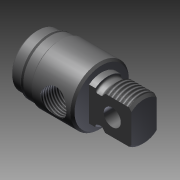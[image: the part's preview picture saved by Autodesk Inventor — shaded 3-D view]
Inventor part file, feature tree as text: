
AUTODESK INVENTOR PART (.ipt)
format: ipt  version: 2011 SP1 (Build 150282100, 282)  size: 287,744 bytes
history: native  units: in
note: dims shown in document units (in); Inventor stores cm internally (conversion verified against a paired STEP export)
features: other x154, sketch x7, revolve x4, thread x2, extrude x2, hole x1
ambient origin geometry x8: Origin, YZ Plane, XZ Plane, XY Plane, X Axis, Y Axis, Z Axis, Center Point
bodies: Solid1 (feature_tree)
feature tree (170):
  revolve  "Revolution1"  Angle=360.0deg
  revolve  "Revolution2"  [1 undecoded]
  thread  "Thread1"  [1 undecoded]
  extrude  "Extrusion1"  TaperAngle=360.0deg  [1 undecoded]
  hole  "Hole1"  [1 undecoded]
  revolve  "Revolution3"  [1 undecoded]
  thread  "Thread2"  [1 undecoded]
  revolve  "Revolution4"  [1 undecoded]
  extrude  "Extrusion2"  [1 undecoded]
  other  "1_XY"
  other  "1_YZ"
  other  "1_ZX"
  other  "1_X"
  other  "1_Y"
  other  "1_Z"
  other  "1_Center"
  other  "c1_XY"
  other  "c1_YZ"
  other  "c1_ZX"
  other  "c1_X"
  other  "c1_Y"
  other  "c1_Z"
  other  "c1_Center"
  other  "c2_XY"
  other  "c2_YZ"
  other  "c2_ZX"
  other  "c2_X"
  other  "c2_Y"
  other  "c2_Z"
  other  "c2_Center"
  other  "cc1_XY"
  other  "cc1_YZ"
  other  "cc1_ZX"
  other  "cc1_X"
  other  "cc1_Y"
  other  "cc1_Z"
  other  "cc1_Center"
  other  "cc2_XY"
  other  "cc2_YZ"
  other  "cc2_ZX"
  other  "cc2_X"
  other  "cc2_Y"
  other  "cc2_Z"
  other  "cc2_Center"
  other  "lovra1_XY"
  other  "lovra1_YZ"
  other  "lovra1_ZX"
  other  "lovra1_X"
  other  "lovra1_Y"
  other  "lovra1_Z"
  other  "lovra1_Center"
  other  "lovra2_XY"
  other  "lovra2_YZ"
  other  "lovra2_ZX"
  other  "lovra2_X"
  other  "lovra2_Y"
  other  "lovra2_Z"
  other  "lovra2_Center"
  other  "lovra21_XY"
  other  "lovra21_YZ"
  other  "lovra21_ZX"
  other  "lovra21_X"
  other  "lovra21_Y"
  other  "lovra21_Z"
  other  "lovra21_Center"
  other  "lovra22_XY"
  other  "lovra22_YZ"
  other  "lovra22_ZX"
  other  "lovra22_X"
  other  "lovra22_Y"
  other  "lovra22_Z"
  other  "lovra22_Center"
  other  "lovra3_XY"
  other  "lovra3_YZ"
  other  "lovra3_ZX"
  other  "lovra3_X"
  other  "lovra3_Y"
  other  "lovra3_Z"
  other  "lovra3_Center"
  other  "olen_XY"
  other  "olen_YZ"
  other  "olen_ZX"
  other  "olen_X"
  other  "olen_Y"
  other  "olen_Z"
  other  "olen_Center"
  other  "p1_XY"
  other  "p1_YZ"
  other  "p1_ZX"
  other  "p1_X"
  other  "p1_Y"
  other  "p1_Z"
  other  "p1_Center"
  other  "p2_XY"
  other  "p2_YZ"
  other  "p2_ZX"
  other  "p2_X"
  other  "p2_Y"
  other  "p2_Z"
  other  "p2_Center"
  other  "port_XY"
  other  "port_YZ"
  other  "port_ZX"
  other  "port_X"
  other  "port_Y"
  other  "port_Z"
  other  "port_Center"
  other  "port2_XY"
  other  "port2_YZ"
  other  "port2_ZX"
  other  "port2_X"
  other  "port2_Y"
  other  "port2_Z"
  other  "port2_Center"
  other  "thd1_XY"
  other  "thd1_YZ"
  other  "thd1_ZX"
  other  "thd1_X"
  other  "thd1_Y"
  other  "thd1_Z"
  other  "thd1_Center"
  other  "thd2_XY"
  other  "thd2_YZ"
  other  "thd2_ZX"
  other  "thd2_X"
  other  "thd2_Y"
  other  "thd2_Z"
  other  "thd2_Center"
  other  "to_mounting_bracket_XY"
  other  "to_mounting_bracket_YZ"
  other  "to_mounting_bracket_ZX"
  other  "to_mounting_bracket_X"
  other  "to_mounting_bracket_Y"
  other  "to_mounting_bracket_Z"
  other  "to_mounting_bracket_Center"
  other  "to_nut_XY"
  other  "to_nut_YZ"
  other  "to_nut_ZX"
  other  "to_nut_X"
  other  "to_nut_Y"
  other  "to_nut_Z"
  other  "to_nut_Center"
  other  "to_pin_XY"
  other  "to_pin_YZ"
  other  "to_pin_ZX"
  other  "to_pin_X"
  other  "to_pin_Y"
  other  "to_pin_Z"
  other  "to_pin_Center"
  other  "to_screw_XY"
  other  "to_screw_YZ"
  other  "to_screw_ZX"
  other  "to_screw_X"
  other  "to_screw_Y"
  other  "to_screw_Z"
  other  "to_screw_Center"
  other  "to_tube_XY"
  other  "to_tube_YZ"
  other  "to_tube_ZX"
  other  "to_tube_X"
  other  "to_tube_Y"
  other  "to_tube_Z"
  other  "to_tube_Center"
  sketch  "Sketch_8"  dims[d2=0.3547in d3=0.0in d4=0.625in d5=0.0in]
  sketch  "Sketch_15"  dims[d14=0.3021in d15=0.0in d16=360.0deg]
  sketch  "Sketch_9"  dims[d6=0.312in d7=0.75in d8=0.375in d9=0.25in d10=0.5635in d11=0.9284in d12=120.0deg d13=360.0deg]
  sketch  "Sketch4"  dims[d0=360.0deg d1=360.0deg]
  sketch  "Sketch_68"
  sketch  "Sketch_24"  dims[d17=0.5587in d18=0.0in d19=0.0in d20=0.0in d21=0.0in d22=0.0in]
  sketch  "Sketch_43"
note: 8 required parameter values undecoded (feature->parameter linkage not recoverable at this tier; creation-order binding heuristic only, values carry confidence <= 0.55)